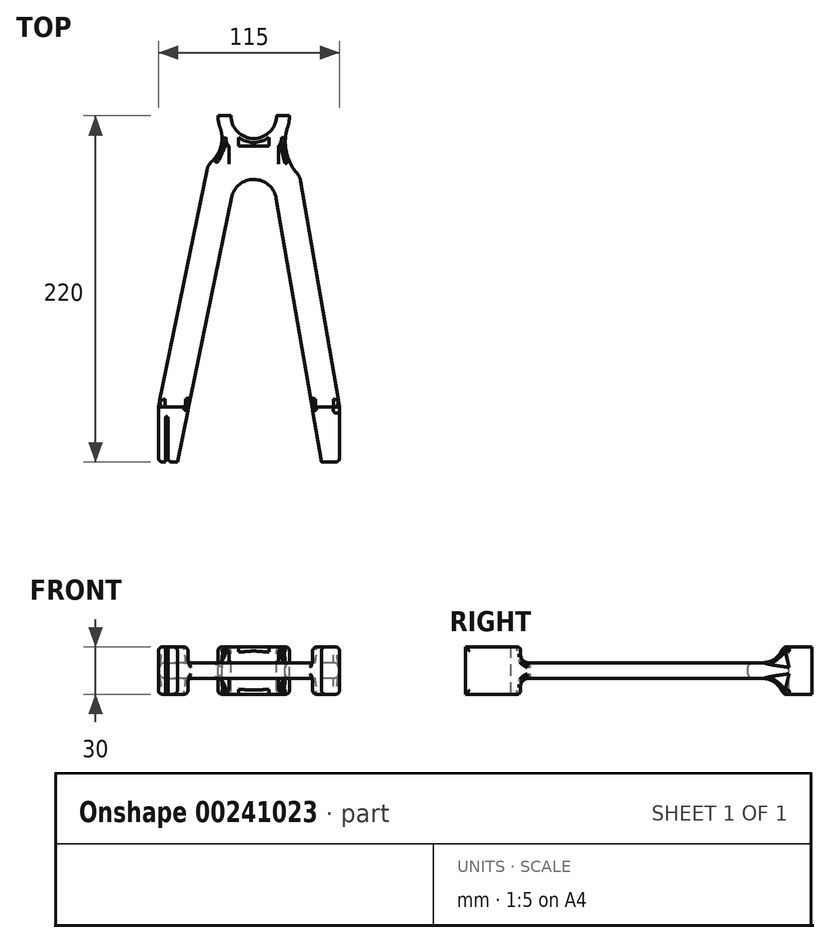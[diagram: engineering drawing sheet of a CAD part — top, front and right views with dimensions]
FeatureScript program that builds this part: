
annotation { "Feature Type Name" : "Feature", "Feature Type Description" : "" }
export const myFeature = defineFeature(function(context is Context, id is Id, definition is map)
    precondition{}
    {
        {
            var Q0;
            Q0=qCreatedBy(makeId("Top.planeOp"),FACE);
            var sketch = newSketch(context, id + "F0", { "sketchPlane" : qUnion([Q0])});
            skArc(sketch, "E0", {"start": v(-14.5, 0) * mm, "mid": v(0, -14.5) * mm, "end": v(14.5, 0) * mm});
            skLineSegment(sketch, "E1", {"start": v(54.5, 0) * mm, "end": v(54.5, -185) * mm, "construction": true});
            skLineSegment(sketch, "E2", {"start": v(29.86, -41.5) * mm, "end": v(54.5, -185) * mm});
            skLineSegment(sketch, "E3", {"start": v(-29.8, -34.63) * mm, "end": v(-60.5, -185) * mm});
            skLineSegment(sketch, "E4", {"start": v(-60.5, -185) * mm, "end": v(-60.5, -220) * mm});
            skLineSegment(sketch, "E5", {"start": v(-60.5, -220) * mm, "end": v(-56.1, -220) * mm});
            skLineSegment(sketch, "E6", {"start": v(54.5, -220) * mm, "end": v(54.5, -185) * mm});
            skLineSegment(sketch, "E7.1", {"start": v(-14.2, -52.1) * mm, "end": v(-48.49, -220) * mm});
            skLineSegment(sketch, "E8.0", {"start": v(14.3, -52.55) * mm, "end": v(43.05, -220) * mm});
            skLineSegment(sketch, "E9.trimOffspring", {"start": v(43.05, -220) * mm, "end": v(54.5, -220) * mm});
            skLineSegment(sketch, "E10", {"start": v(-22.73, 0) * mm, "end": v(-14.5, 0) * mm});
            skLineSegment(sketch, "E11", {"start": v(14.5, 0) * mm, "end": v(22.73, 0) * mm});
            skLineSegment(sketch, "E12", {"start": v(-56.1, -220) * mm, "end": v(-56.1, -192) * mm});
            skLineSegment(sketch, "E13", {"start": v(-54.5, -192) * mm, "end": v(-54.5, -220) * mm});
            skLineSegment(sketch, "E14.trimOffspring", {"start": v(-54.5, -220) * mm, "end": v(-48.49, -220) * mm});
            skArc(sketch, "E15", {"start": v(-54.5, -192) * mm, "mid": v(-55.3, -191.2) * mm, "end": v(-56.1, -192) * mm});
            skArc(sketch, "E16.filletArc", {"start": v(14.3, -52.55) * mm, "mid": v(0.23, -40.5) * mm, "end": v(-14.2, -52.1) * mm});
            skArc(sketch, "E17", {"start": v(-22.73, 0) * mm, "mid": v(-22.38, -3.93) * mm, "end": v(-21.37, -7.75) * mm});
            skArc(sketch, "E18", {"start": v(-26.7, -29.21) * mm, "mid": v(-20.76, -19.3) * mm, "end": v(-21.37, -7.75) * mm});
            skArc(sketch, "E19", {"start": v(21.55, -7.22) * mm, "mid": v(20.6, -22.7) * mm, "end": v(27.5, -36.58) * mm});
            skArc(sketch, "E20.trimOffspring", {"start": v(21.55, -7.22) * mm, "mid": v(22.43, -3.66) * mm, "end": v(22.73, 0) * mm});
            skPoint(sketch, "E21.visualSharp", {"position": v(-29.07, -31.04) * mm});
            skArc(sketch, "E21.filletArc", {"start": v(-26.7, -29.21) * mm, "mid": v(-28.69, -31.67) * mm, "end": v(-29.8, -34.63) * mm});
            skPoint(sketch, "E22.visualSharp", {"position": v(29.34, -38.49) * mm});
            skArc(sketch, "E22.filletArc", {"start": v(29.86, -41.5) * mm, "mid": v(29.02, -38.88) * mm, "end": v(27.5, -36.58) * mm});
            skSolve(sketch);
        }
        {
            var Q0;
            Q0 = qSketchRegion(id + "F0", true);
            extrude(context, id + "F1", {"entities" : qUnion([Q0]), "endBound" : BoundingType.SYMMETRIC, "oppositeDirection" : true, "depth" : 30 * mm});
        }
        {
            var Q0;
            Q0=makeQuery(id+"F1.opExtrude","SWEPT_EDGE",EDGE,{"disambiguationData":[OSD([sQuery(id+"F0.wireOp",EDGE,"E4"),sQuery(id+"F0.wireOp",EDGE,"E5")])]});
            var Q1;
            Q1=makeQuery(id+"F1.opExtrude","SWEPT_EDGE",EDGE,{"disambiguationData":[OSD([sQuery(id+"F0.wireOp",EDGE,"E6"),sQuery(id+"F0.wireOp",EDGE,"E9.trimOffspring")])]});
            var Q2;
            Q2=makeQuery(id+"F1.opExtrude","SWEPT_EDGE",EDGE,{"disambiguationData":[OSD([sQuery(id+"F0.wireOp",EDGE,"E2"),sQuery(id+"F0.wireOp",EDGE,"E6")])]});
            var Q3;
            Q3=makeQuery(id+"F1.opExtrude","SWEPT_EDGE",EDGE,{"disambiguationData":[OSD([sQuery(id+"F0.wireOp",EDGE,"E3"),sQuery(id+"F0.wireOp",EDGE,"E4")])]});
            var Q4;
            Q4=makeQuery(id+"F1.opExtrude","SWEPT_EDGE",EDGE,{"disambiguationData":[OSD([sQuery(id+"F0.wireOp",EDGE,"E13"),sQuery(id+"F0.wireOp",EDGE,"E14.trimOffspring")])]});
            var Q5;
            Q5=makeQuery(id+"F1.opExtrude","CAP_EDGE",EDGE,{"disambiguationData":[OSD([sQuery(id+"F0.wireOp",EDGE,"E7.1")])],"isStart":true});
            var Q6;
            Q6=makeQuery(id+"F1.opExtrude","CAP_EDGE",EDGE,{"disambiguationData":[OSD([sQuery(id+"F0.wireOp",EDGE,"E7.0")])],"isStart":true});
            var Q7;
            Q7=makeQuery(id+"F1.opExtrude","CAP_EDGE",EDGE,{"disambiguationData":[OSD([sQuery(id+"F0.wireOp",EDGE,"1f4d6002-adc0-4d8f-b84d-65dcdfc4606f.0")])],"isStart":true});
            var Q8;
            Q8=makeQuery(id+"F1.opExtrude","CAP_EDGE",EDGE,{"disambiguationData":[OSD([sQuery(id+"F0.wireOp",EDGE,"E8.0")])],"isStart":true});
            var Q9;
            Q9=makeQuery(id+"F1.opExtrude","CAP_EDGE",EDGE,{"disambiguationData":[OSD([sQuery(id+"F0.wireOp",EDGE,"E8.0")])],"isStart":false});
            var Q10;
            Q10=makeQuery(id+"F1.opExtrude","CAP_EDGE",EDGE,{"disambiguationData":[OSD([sQuery(id+"F0.wireOp",EDGE,"1f4d6002-adc0-4d8f-b84d-65dcdfc4606f.0")])],"isStart":false});
            var Q11;
            Q11=makeQuery(id+"F1.opExtrude","CAP_EDGE",EDGE,{"disambiguationData":[OSD([sQuery(id+"F0.wireOp",EDGE,"E6")])],"isStart":true});
            var Q12;
            Q12=makeQuery(id+"F1.opExtrude","CAP_EDGE",EDGE,{"disambiguationData":[OSD([sQuery(id+"F0.wireOp",EDGE,"E2")])],"isStart":true});
            var Q13;
            Q13=makeQuery(id+"F1.opExtrude","CAP_EDGE",EDGE,{"disambiguationData":[OSD([sQuery(id+"F0.wireOp",EDGE,"E3")])],"isStart":true});
            var Q14;
            Q14=makeQuery(id+"F1.opExtrude","CAP_EDGE",EDGE,{"disambiguationData":[OSD([sQuery(id+"F0.wireOp",EDGE,"E3")])],"isStart":false});
            var Q15;
            Q15=makeQuery(id+"F1.opExtrude","CAP_EDGE",EDGE,{"disambiguationData":[OSD([sQuery(id+"F0.wireOp",EDGE,"E4")])],"isStart":true});
            var Q16;
            Q16=makeQuery(id+"F1.opExtrude","CAP_EDGE",EDGE,{"disambiguationData":[OSD([sQuery(id+"F0.wireOp",EDGE,"E2")])],"isStart":false});
            var Q17;
            Q17=makeQuery(id+"F1.opExtrude","CAP_EDGE",EDGE,{"disambiguationData":[OSD([sQuery(id+"F0.wireOp",EDGE,"E6")])],"isStart":false});
            var Q18;
            Q18=makeQuery(id+"F1.opExtrude","CAP_EDGE",EDGE,{"disambiguationData":[OSD([sQuery(id+"F0.wireOp",EDGE,"E7.1")])],"isStart":false});
            var Q19;
            Q19=makeQuery(id+"F1.opExtrude","CAP_EDGE",EDGE,{"disambiguationData":[OSD([sQuery(id+"F0.wireOp",EDGE,"E7.0")])],"isStart":false});
            var Q20;
            Q20=makeQuery(id+"F1.opExtrude","CAP_EDGE",EDGE,{"disambiguationData":[OSD([sQuery(id+"F0.wireOp",EDGE,"E0")])],"isStart":false});
            var Q21;
            Q21=makeQuery(id+"F1.opExtrude","CAP_EDGE",EDGE,{"disambiguationData":[OSD([sQuery(id+"F0.wireOp",EDGE,"E0")])],"isStart":true});
            var Q22;
            Q22=makeQuery(id+"F1.opExtrude","CAP_EDGE",EDGE,{"disambiguationData":[OSD([sQuery(id+"F0.wireOp",EDGE,"LkaVHIsl-Z9kB-naX4-EJHS-kliyvRkEoExY")])],"isStart":false});
            var Q23;
            Q23=makeQuery(id+"F1.opExtrude","CAP_EDGE",EDGE,{"disambiguationData":[OSD([sQuery(id+"F0.wireOp",EDGE,"LkaVHIsl-Z9kB-naX4-EJHS-kliyvRkEoExY")])],"isStart":true});
            var Q24;
            Q24=makeQuery(id+"F1.opExtrude","CAP_EDGE",EDGE,{"disambiguationData":[OSD([sQuery(id+"F0.wireOp",EDGE,"E4")])],"isStart":false});
            fillet(context, id + "F2", {"entities" : qUnion([Q0, Q1, Q2, Q3, Q4, Q5, Q6, Q7, Q8, Q9, Q10, Q11, Q12, Q13, Q14, Q15, Q16, Q17, Q18, Q19, Q20, Q21, Q22, Q23, Q24]), "radius" : 2.5 * mm, "tangentPropagation" : true, "allowEdgeOverflow" : false});
        }
        {
            var Q0;
            Q0=qCreatedBy(makeId("Right.planeOp"),FACE);
            var sketch = newSketch(context, id + "F3", { "sketchPlane" : qUnion([Q0])});
            skLineSegment(sketch, "E23.bottom", {"start": v(-185, 15) * mm, "end": v(-20, 15) * mm});
            skLineSegment(sketch, "E23.top", {"start": v(-185, 5) * mm, "end": v(-20, 5) * mm});
            skLineSegment(sketch, "E23.left", {"start": v(-185, 15) * mm, "end": v(-185, 5) * mm});
            skLineSegment(sketch, "E23.right", {"start": v(-20, 15) * mm, "end": v(-20, 5) * mm});
            skLineSegment(sketch, "E24.bottom", {"start": v(-185, -15) * mm, "end": v(-20, -15) * mm});
            skLineSegment(sketch, "E24.top", {"start": v(-185, -5) * mm, "end": v(-20, -5) * mm});
            skLineSegment(sketch, "E24.left", {"start": v(-185, -15) * mm, "end": v(-185, -5) * mm});
            skLineSegment(sketch, "E24.right", {"start": v(-20, -15) * mm, "end": v(-20, -5) * mm});
            skPoint(sketch, "E25.visualSharp", {"position": v(-20, -5) * mm});
            skPoint(sketch, "E26.visualSharp", {"position": v(-185, 5) * mm});
            skLineSegment(sketch, "E27", {"start": v(-20, 5) * mm, "end": v(-20, -5) * mm, "construction": true});
            skLineSegment(sketch, "E28", {"start": v(-185, 5) * mm, "end": v(-185, -5) * mm});
            skSolve(sketch);
        }
        {
            var Q0;
            Q0 = qSketchRegion(id + "F3", true);
            extrude(context, id + "F4", {"entities" : qUnion([Q0]), "operationType" : NewBodyOperationType.REMOVE, "endBound" : BoundingType.SYMMETRIC, "depth" : 200 * mm});
        }
        {
            var Q0;
            Q0=makeQuery(id+"F4.boolean.opBoolean","INTERSECT",EDGE,{"derivedFrom":[makeQuery(id+"F1.opExtrude","SWEPT_FACE",FACE,{"disambiguationData":[OSD([sQuery(id+"F0.wireOp",EDGE,"E8.0")])]}),makeQuery(id+"F4.opExtrude","SWEPT_FACE",FACE,{"disambiguationData":[OSD([sQuery(id+"F3.wireOp",EDGE,"E24.top")])]})]});
            var Q1;
            Q1=makeQuery(id+"F4.boolean.opBoolean","INTERSECT",EDGE,{"derivedFrom":[makeQuery(id+"F1.opExtrude","SWEPT_FACE",FACE,{"disambiguationData":[OSD([sQuery(id+"F0.wireOp",EDGE,"E2")])]}),makeQuery(id+"F4.opExtrude","SWEPT_FACE",FACE,{"disambiguationData":[OSD([sQuery(id+"F3.wireOp",EDGE,"E24.top")])]})]});
            var Q2;
            Q2=makeQuery(id+"F4.boolean.opBoolean","INTERSECT",EDGE,{"derivedFrom":[makeQuery(id+"F1.opExtrude","SWEPT_FACE",FACE,{"disambiguationData":[OSD([sQuery(id+"F0.wireOp",EDGE,"E3")])]}),makeQuery(id+"F4.opExtrude","SWEPT_FACE",FACE,{"disambiguationData":[OSD([sQuery(id+"F3.wireOp",EDGE,"E24.top")])]})]});
            var Q3;
            Q3=makeQuery(id+"F4.boolean.opBoolean","INTERSECT",EDGE,{"derivedFrom":[makeQuery(id+"F1.opExtrude","SWEPT_FACE",FACE,{"disambiguationData":[OSD([sQuery(id+"F0.wireOp",EDGE,"E3")])]}),makeQuery(id+"F4.opExtrude","SWEPT_FACE",FACE,{"disambiguationData":[OSD([sQuery(id+"F3.wireOp",EDGE,"E23.top")])]})]});
            var Q4;
            Q4=makeQuery(id+"F4.boolean.opBoolean","INTERSECT",EDGE,{"derivedFrom":[makeQuery(id+"F1.opExtrude","SWEPT_FACE",FACE,{"disambiguationData":[OSD([sQuery(id+"F0.wireOp",EDGE,"E7.1")])]}),makeQuery(id+"F4.opExtrude","SWEPT_FACE",FACE,{"disambiguationData":[OSD([sQuery(id+"F3.wireOp",EDGE,"E23.top")])]})]});
            var Q5;
            Q5=makeQuery(id+"F4.boolean.opBoolean","INTERSECT",EDGE,{"derivedFrom":[makeQuery(id+"F1.opExtrude","SWEPT_FACE",FACE,{"disambiguationData":[OSD([sQuery(id+"F0.wireOp",EDGE,"E2")])]}),makeQuery(id+"F4.opExtrude","SWEPT_FACE",FACE,{"disambiguationData":[OSD([sQuery(id+"F3.wireOp",EDGE,"E23.top")])]})]});
            fillet(context, id + "F5", {"entities" : qUnion([Q0, Q1, Q2, Q3, Q4, Q5]), "radius" : 3 * mm, "tangentPropagation" : true, "allowEdgeOverflow" : false});
        }
        {
            var Q0;
            Q0=makeQuery(id+"F4.boolean.opBoolean","INTERSECT",EDGE,{"derivedFrom":[makeQuery(id+"F1.opExtrude","SWEPT_FACE",FACE,{"disambiguationData":[OSD([sQuery(id+"F0.wireOp",EDGE,"E19")])]}),makeQuery(id+"F4.opExtrude","SWEPT_FACE",FACE,{"disambiguationData":[OSD([sQuery(id+"F3.wireOp",EDGE,"E23.right")])]})]});
            var Q1;
            Q1=makeQuery(id+"F4.boolean.opBoolean","INTERSECT",EDGE,{"derivedFrom":[makeQuery(id+"F1.opExtrude","SWEPT_FACE",FACE,{"disambiguationData":[OSD([sQuery(id+"F0.wireOp",EDGE,"E19")])]}),makeQuery(id+"F4.opExtrude","SWEPT_FACE",FACE,{"disambiguationData":[OSD([sQuery(id+"F3.wireOp",EDGE,"E24.right")])]})]});
            fillet(context, id + "F6", {"entities" : qUnion([Q0, Q1]), "radius" : 6 * mm, "tangentPropagation" : true, "allowEdgeOverflow" : false});
        }
        {
            var Q0;
            {var subQ0=sQuery(id+"F3.wireOp",EDGE,"E24.top");var subQ1=sQuery(id+"F3.wireOp",EDGE,"E24.left");Q0=makeQuery(id+"F4.boolean.opBoolean","COPY",EDGE,{"disambiguationData":[TD([makeQuery(id+"F1.opExtrude","SWEPT_FACE",FACE,{"disambiguationData":[OSD([sQuery(id+"F0.wireOp",EDGE,"E7.1")])]})])],"derivedFrom":makeQuery(id+"F4.opExtrude","SWEPT_EDGE",EDGE,{"disambiguationData":[OSD([subQ0,subQ1])]})});}
            var Q1;
            {var subQ2=sQuery(id+"F3.wireOp",EDGE,"E23.top");var subQ3=sQuery(id+"F3.wireOp",EDGE,"E23.left");Q1=makeQuery(id+"F4.boolean.opBoolean","COPY",EDGE,{"disambiguationData":[TD([makeQuery(id+"F1.opExtrude","SWEPT_FACE",FACE,{"disambiguationData":[OSD([sQuery(id+"F0.wireOp",EDGE,"E7.1")])]})])],"derivedFrom":makeQuery(id+"F4.opExtrude","SWEPT_EDGE",EDGE,{"disambiguationData":[OSD([subQ2,subQ3])]})});}
            var Q2;
            {var subQ0=sQuery(id+"F3.wireOp",EDGE,"E23.top");var subQ1=sQuery(id+"F3.wireOp",EDGE,"E23.left");Q2=makeQuery(id+"F4.boolean.opBoolean","COPY",EDGE,{"disambiguationData":[TD([makeQuery(id+"F1.opExtrude","SWEPT_FACE",FACE,{"disambiguationData":[OSD([sQuery(id+"F0.wireOp",EDGE,"E8.0")])]})])],"derivedFrom":makeQuery(id+"F4.opExtrude","SWEPT_EDGE",EDGE,{"disambiguationData":[OSD([subQ0,subQ1])]})});}
            var Q3;
            {var subQ2=sQuery(id+"F3.wireOp",EDGE,"E24.top");var subQ3=sQuery(id+"F3.wireOp",EDGE,"E24.left");Q3=makeQuery(id+"F4.boolean.opBoolean","COPY",EDGE,{"disambiguationData":[TD([makeQuery(id+"F1.opExtrude","SWEPT_FACE",FACE,{"disambiguationData":[OSD([sQuery(id+"F0.wireOp",EDGE,"E8.0")])]})])],"derivedFrom":makeQuery(id+"F4.opExtrude","SWEPT_EDGE",EDGE,{"disambiguationData":[OSD([subQ2,subQ3])]})});}
            fillet(context, id + "F7", {"entities" : qUnion([Q0, Q1, Q2, Q3]), "radius" : 5 * mm, "tangentPropagation" : true, "allowEdgeOverflow" : false});
        }
        {
            var Q0;
            {var subQ1=sQuery(id+"F0.wireOp",EDGE,"E3");var subQ2=sQuery(id+"F3.wireOp",EDGE,"E23.left");Q0=makeQuery(id+"F4.boolean.opBoolean","COPY",EDGE,{"disambiguationData":[TD([makeQuery(id+"F2.opFillet","BLEND_FACE",FACE,{"disambiguationData":[OSD([subQ1]),TDD([makeQuery(id+"F1.opExtrude","CAP_EDGE",EDGE,{"disambiguationData":[OSD([subQ1])],"isStart":true})])]})])],"derivedFrom":makeQuery(id+"F4.opExtrude","SWEPT_EDGE",EDGE,{"disambiguationData":[OSD([sQuery(id+"F3.wireOp",EDGE,"E23.bottom"),subQ2])]})});}
            var Q1;
            {var subQ1=sQuery(id+"F0.wireOp",EDGE,"E2");var subQ2=sQuery(id+"F3.wireOp",EDGE,"E23.left");Q1=makeQuery(id+"F4.boolean.opBoolean","COPY",EDGE,{"disambiguationData":[TD([makeQuery(id+"F2.opFillet","BLEND_FACE",FACE,{"disambiguationData":[OSD([subQ1]),TDD([makeQuery(id+"F1.opExtrude","CAP_EDGE",EDGE,{"disambiguationData":[OSD([subQ1])],"isStart":true})])]})])],"derivedFrom":makeQuery(id+"F4.opExtrude","SWEPT_EDGE",EDGE,{"disambiguationData":[OSD([sQuery(id+"F3.wireOp",EDGE,"E23.bottom"),subQ2])]})});}
            var Q2;
            {var subQ1=sQuery(id+"F0.wireOp",EDGE,"E2");var subQ2=sQuery(id+"F3.wireOp",EDGE,"E24.left");Q2=makeQuery(id+"F4.boolean.opBoolean","COPY",EDGE,{"disambiguationData":[TD([makeQuery(id+"F2.opFillet","BLEND_FACE",FACE,{"disambiguationData":[OSD([subQ1]),TDD([makeQuery(id+"F1.opExtrude","CAP_EDGE",EDGE,{"disambiguationData":[OSD([subQ1])],"isStart":false})])]})])],"derivedFrom":makeQuery(id+"F4.opExtrude","SWEPT_EDGE",EDGE,{"disambiguationData":[OSD([sQuery(id+"F3.wireOp",EDGE,"E24.bottom"),subQ2])]})});}
            var Q3;
            {var subQ1=sQuery(id+"F0.wireOp",EDGE,"E3");var subQ2=sQuery(id+"F3.wireOp",EDGE,"E24.left");Q3=makeQuery(id+"F4.boolean.opBoolean","COPY",EDGE,{"disambiguationData":[TD([makeQuery(id+"F2.opFillet","BLEND_FACE",FACE,{"disambiguationData":[OSD([subQ1]),TDD([makeQuery(id+"F1.opExtrude","CAP_EDGE",EDGE,{"disambiguationData":[OSD([subQ1])],"isStart":false})])]})])],"derivedFrom":makeQuery(id+"F4.opExtrude","SWEPT_EDGE",EDGE,{"disambiguationData":[OSD([sQuery(id+"F3.wireOp",EDGE,"E24.bottom"),subQ2])]})});}
            fillet(context, id + "F8", {"entities" : qUnion([Q0, Q1, Q2, Q3]), "radius" : 2 * mm, "tangentPropagation" : true, "allowEdgeOverflow" : false});
        }
        {
            var Q0;
            Q0=makeQuery(id+"F4.boolean.opBoolean","COPY",EDGE,{"derivedFrom":makeQuery(id+"F4.opExtrude","SWEPT_EDGE",EDGE,{"disambiguationData":[OSD([sQuery(id+"F3.wireOp",EDGE,"E23.top"),sQuery(id+"F3.wireOp",EDGE,"E23.right")])]})});
            var Q1;
            Q1=makeQuery(id+"F4.boolean.opBoolean","COPY",EDGE,{"derivedFrom":makeQuery(id+"F4.opExtrude","SWEPT_EDGE",EDGE,{"disambiguationData":[OSD([sQuery(id+"F3.wireOp",EDGE,"E24.top"),sQuery(id+"F3.wireOp",EDGE,"E24.right")])]})});
            fillet(context, id + "F9", {"entities" : qUnion([Q0, Q1]), "radius" : 13 * mm, "tangentPropagation" : true, "allowEdgeOverflow" : false});
        }
    });
